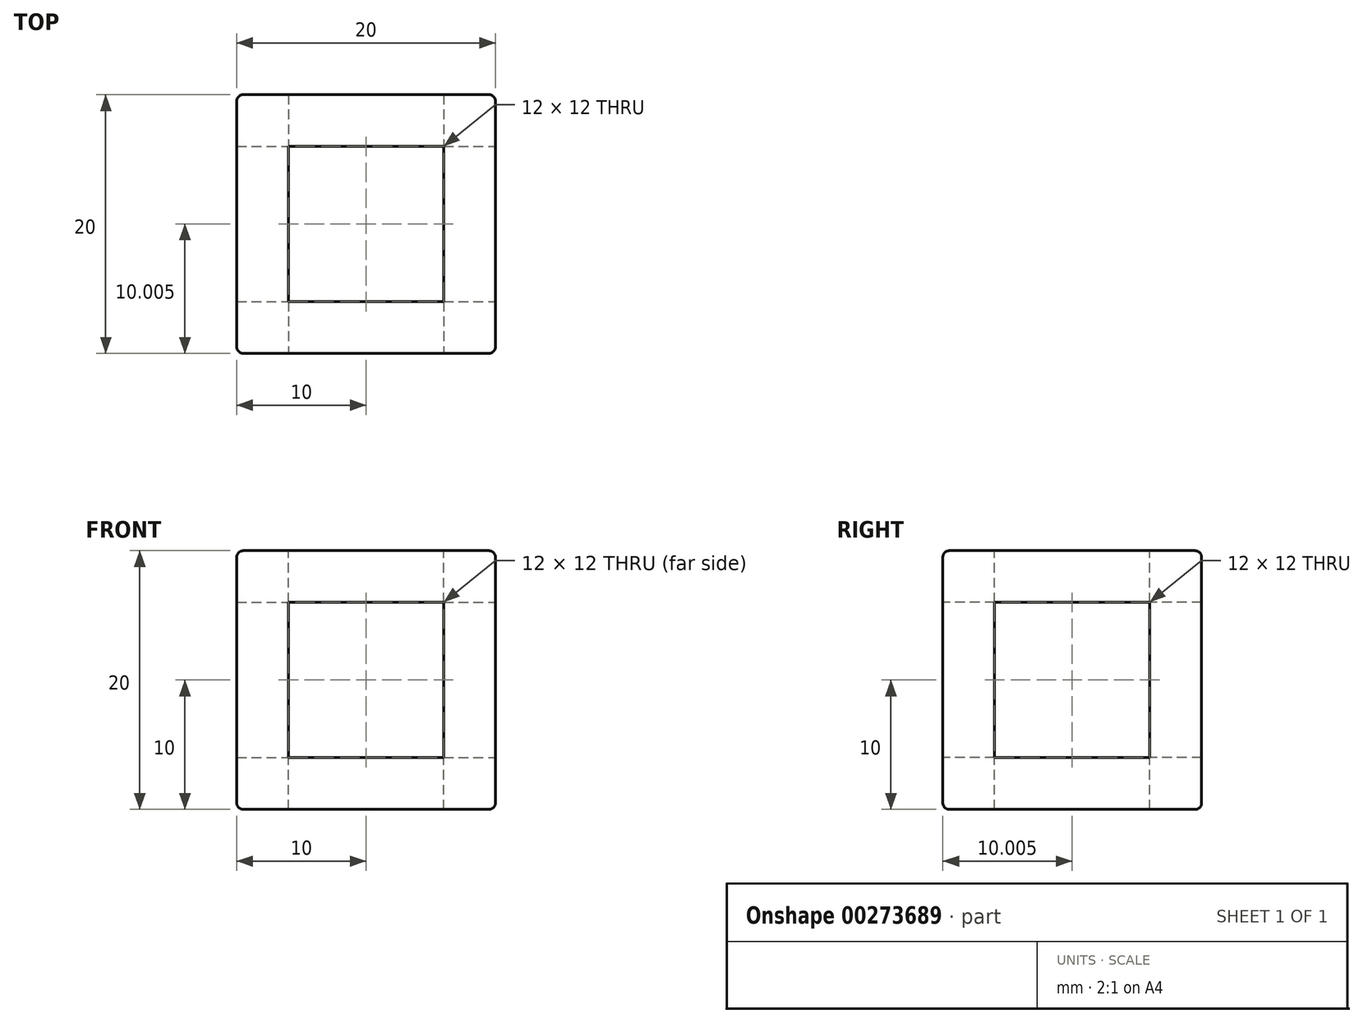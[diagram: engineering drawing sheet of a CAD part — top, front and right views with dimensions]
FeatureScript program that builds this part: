
annotation { "Feature Type Name" : "Feature", "Feature Type Description" : "" }
export const myFeature = defineFeature(function(context is Context, id is Id, definition is map)
    precondition{}
    {
        {
            var Q0;
            Q0=qCreatedBy(makeId("Top.planeOp"),FACE);
            var sketch = newSketch(context, id + "F0", { "sketchPlane" : qUnion([Q0])});
            skLineSegment(sketch, "E0.bottom", {"start": v(-8.9, 10.04) * mm, "end": v(11.1, 10.04) * mm});
            skLineSegment(sketch, "E0.top", {"start": v(-8.9, -9.96) * mm, "end": v(11.1, -9.96) * mm});
            skLineSegment(sketch, "E0.left", {"start": v(-8.9, 10.04) * mm, "end": v(-8.9, -9.96) * mm});
            skLineSegment(sketch, "E0.right", {"start": v(11.1, 10.04) * mm, "end": v(11.1, -9.96) * mm});
            skSolve(sketch);
        }
        {
            var Q0;
            Q0=makeQuery(id+"F0.imprint","IMPRINT",FACE,{"disambiguationData":[TD([[makeQuery(id+"F0.imprint","IMPRINT",EDGE,{"derivedFrom":sQuery(id+"F0.wireOp",EDGE,"E0.bottom")}),-1.0]])]});
            extrude(context, id + "F1", {"entities" : qUnion([Q0]), "depth" : 20 * mm});
        }
        {
            var Q0;
            Q0=makeQuery(id+"F1.opExtrude","CAP_FACE",FACE,{"disambiguationData":[OSD([sQuery(id+"F0.wireOp",EDGE,"E0.bottom"),sQuery(id+"F0.wireOp",EDGE,"E0.top"),sQuery(id+"F0.wireOp",EDGE,"E0.left"),sQuery(id+"F0.wireOp",EDGE,"E0.right")])],"isStart":false});
            var sketch = newSketch(context, id + "F2", { "sketchPlane" : qUnion([Q0])});
            skLineSegment(sketch, "E1.bottom", {"start": v(-4.9, 6.04) * mm, "end": v(7.1, 6.04) * mm});
            skLineSegment(sketch, "E1.top", {"start": v(-4.9, -5.96) * mm, "end": v(7.1, -5.96) * mm});
            skLineSegment(sketch, "E1.left", {"start": v(-4.9, 6.04) * mm, "end": v(-4.9, -5.96) * mm});
            skLineSegment(sketch, "E1.right", {"start": v(7.1, 6.04) * mm, "end": v(7.1, -5.96) * mm});
            skSolve(sketch);
        }
        {
            var Q0;
            Q0 = qSketchRegion(id + "F2", true);
            extrude(context, id + "F3", {"entities" : qUnion([Q0]), "operationType" : NewBodyOperationType.REMOVE, "oppositeDirection" : true, "depth" : 25 * mm});
        }
        {
            var Q0;
            Q0=makeQuery(id+"F1.opExtrude","SWEPT_FACE",FACE,{"disambiguationData":[OSD([sQuery(id+"F0.wireOp",EDGE,"E0.right")])]});
            var sketch = newSketch(context, id + "F4", { "sketchPlane" : qUnion([Q0])});
            skLineSegment(sketch, "E2.bottom", {"start": v(6.04, 16) * mm, "end": v(-5.96, 16) * mm});
            skLineSegment(sketch, "E2.top", {"start": v(6.04, 4) * mm, "end": v(-5.96, 4) * mm});
            skLineSegment(sketch, "E2.left", {"start": v(6.04, 16) * mm, "end": v(6.04, 4) * mm});
            skLineSegment(sketch, "E2.right", {"start": v(-5.96, 16) * mm, "end": v(-5.96, 4) * mm});
            skSolve(sketch);
        }
        {
            var Q0;
            Q0 = qSketchRegion(id + "F4", true);
            var Q1;
            Q1=makeQuery(id+"F4.imprint","IMPRINT",FACE,{"disambiguationData":[TD([[makeQuery(id+"F4.imprint","IMPRINT",EDGE,{"derivedFrom":sQuery(id+"F4.wireOp",EDGE,"E2.bottom")}),1.0]])]});
            extrude(context, id + "F5", {"entities" : qUnion([Q0, Q1]), "operationType" : NewBodyOperationType.REMOVE, "oppositeDirection" : true, "depth" : 25 * mm});
        }
        {
            var Q0;
            Q0=makeQuery(id+"F1.opExtrude","SWEPT_FACE",FACE,{"disambiguationData":[OSD([sQuery(id+"F0.wireOp",EDGE,"E0.top")])]});
            var sketch = newSketch(context, id + "F6", { "sketchPlane" : qUnion([Q0])});
            skLineSegment(sketch, "E3.bottom", {"start": v(-4.9, 16) * mm, "end": v(7.1, 16) * mm});
            skLineSegment(sketch, "E3.top", {"start": v(-4.9, 4) * mm, "end": v(7.1, 4) * mm});
            skLineSegment(sketch, "E3.left", {"start": v(-4.9, 16) * mm, "end": v(-4.9, 4) * mm});
            skLineSegment(sketch, "E3.right", {"start": v(7.1, 16) * mm, "end": v(7.1, 4) * mm});
            skSolve(sketch);
        }
        {
            var Q0;
            Q0=makeQuery(id+"F6.imprint","IMPRINT",FACE,{"disambiguationData":[TD([[makeQuery(id+"F6.imprint","IMPRINT",EDGE,{"derivedFrom":sQuery(id+"F6.wireOp",EDGE,"E3.bottom")}),-1.0]])]});
            extrude(context, id + "F7", {"entities" : qUnion([Q0]), "operationType" : NewBodyOperationType.REMOVE, "oppositeDirection" : true, "depth" : 25 * mm});
        }
        {
            var Q0;
            Q0=makeQuery(id+"F1.opExtrude","CAP_EDGE",EDGE,{"disambiguationData":[OSD([sQuery(id+"F0.wireOp",EDGE,"E0.top")])],"isStart":false});
            fillet(context, id + "F8", {"entities" : qUnion([Q0]), "radius" : 0.5 * mm, "tangentPropagation" : true, "allowEdgeOverflow" : false});
        }
        {
            var Q0;
            Q0=makeQuery(id+"F1.opExtrude","CAP_EDGE",EDGE,{"disambiguationData":[OSD([sQuery(id+"F0.wireOp",EDGE,"E0.right")])],"isStart":false});
            fillet(context, id + "F9", {"entities" : qUnion([Q0]), "radius" : 0.5 * mm, "tangentPropagation" : true, "allowEdgeOverflow" : false});
        }
        {
            var Q0;
            Q0=makeQuery(id+"F1.opExtrude","SWEPT_EDGE",EDGE,{"disambiguationData":[OSD([sQuery(id+"F0.wireOp",EDGE,"E0.top"),sQuery(id+"F0.wireOp",EDGE,"E0.left")])]});
            fillet(context, id + "F10", {"entities" : qUnion([Q0]), "radius" : 0.5 * mm, "tangentPropagation" : true, "allowEdgeOverflow" : false});
        }
        {
            var Q0;
            Q0=makeQuery(id+"F1.opExtrude","CAP_EDGE",EDGE,{"disambiguationData":[OSD([sQuery(id+"F0.wireOp",EDGE,"E0.top")])],"isStart":true});
            fillet(context, id + "F11", {"entities" : qUnion([Q0]), "radius" : 0.5 * mm, "tangentPropagation" : true, "allowEdgeOverflow" : false});
        }
        {
            var Q0;
            Q0=makeQuery(id+"F1.opExtrude","SWEPT_EDGE",EDGE,{"disambiguationData":[OSD([sQuery(id+"F0.wireOp",EDGE,"E0.bottom"),sQuery(id+"F0.wireOp",EDGE,"E0.left")])]});
            fillet(context, id + "F12", {"entities" : qUnion([Q0]), "radius" : 0.5 * mm, "tangentPropagation" : true, "allowEdgeOverflow" : false});
        }
    });
